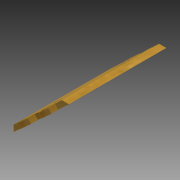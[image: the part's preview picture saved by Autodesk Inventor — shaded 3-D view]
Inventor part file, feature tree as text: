
AUTODESK INVENTOR PART (.ipt)
format: ipt  version: 2014 (Build 180170000, 170)  size: 153,088 bytes
history: native  units: mm
features: extrude x5, sketch x4
ambient origin geometry x8: Origin, YZ Plane, XZ Plane, XY Plane, X Axis, Y Axis, Z Axis, Center Point
bodies: Solid1 (feature_tree)
feature tree (9):
  extrude  "Extrusion1"  Depth=70.0mm TaperAngle=0.0deg
  sketch  "Sketch2"  dims[d7=25.0mm d8=5.0mm]
  extrude  "Extrusion2"  Depth=5.0mm
  extrude  "Extrusion3"  Depth=10.0mm
  extrude  "Extrusion4"  Depth=2.0mm
  extrude  "Extrusion5"  Depth=5.0mm
  sketch  "Sketch1"  dims[d2=5.0mm d5=70.0mm d6=0.0mm]
  sketch  "Sketch3"  dims[d9=10.0mm d10=1.5mm]
  sketch  "Sketch4"  dims[d11=8.0mm d12=2.0mm d13=5.0mm d14=7.0mm d15=2.0mm d16=35.0mm d17=5.0mm d18=0.0mm d19=5.0mm d20=0.0mm d25=90.0deg d28=10.0mm d32=18.45659mm d33=10.0mm d34=5.0mm d35=0.0mm d41=5.0mm d42=0.0mm d46=32.5mm]
